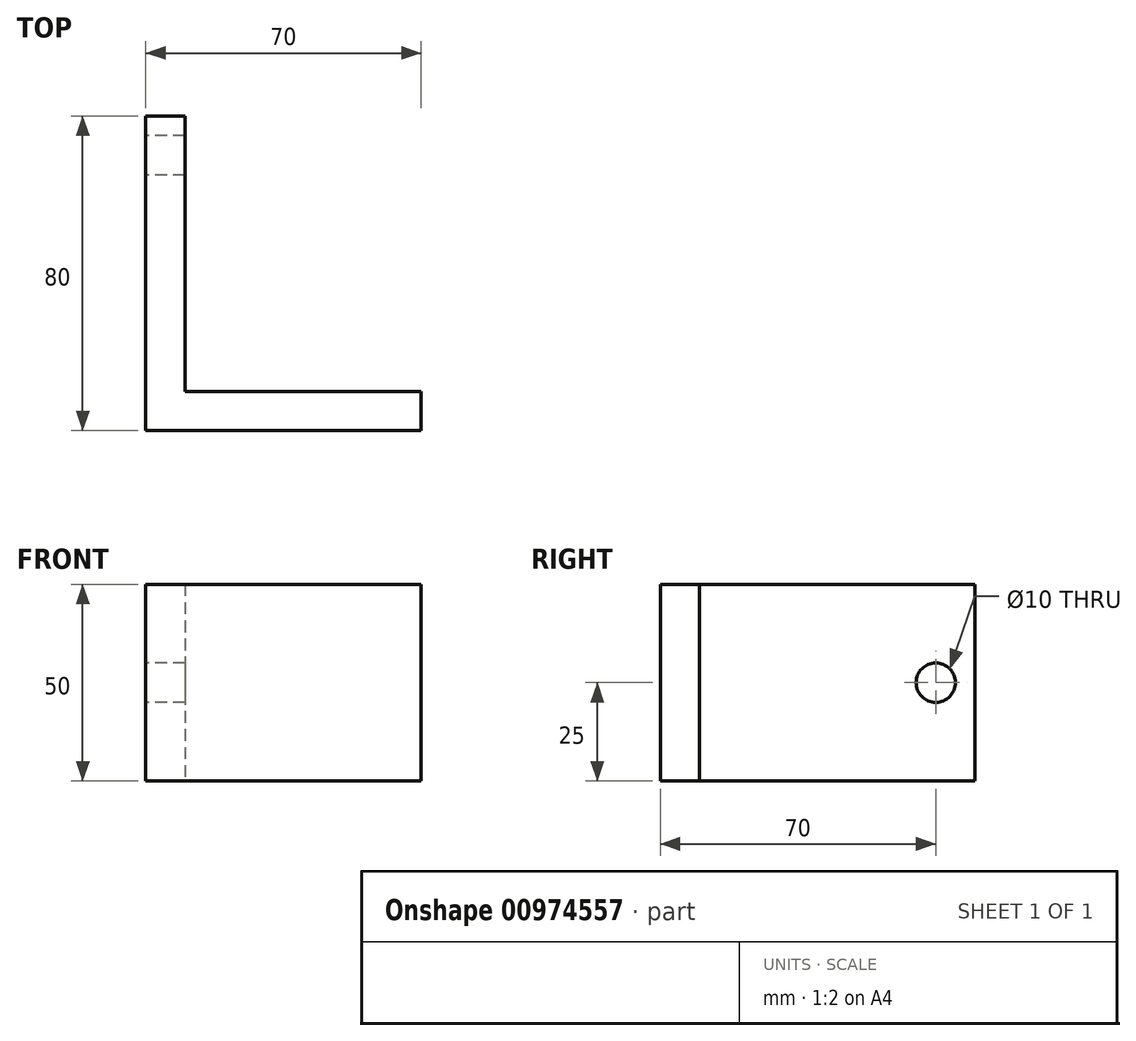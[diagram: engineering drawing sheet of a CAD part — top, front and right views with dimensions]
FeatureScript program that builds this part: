
annotation { "Feature Type Name" : "Feature", "Feature Type Description" : "" }
export const myFeature = defineFeature(function(context is Context, id is Id, definition is map)
    precondition{}
    {
        {
            var Q0;
            Q0=qCreatedBy(makeId("Front.planeOp"),FACE);
            var sketch = newSketch(context, id + "F0", { "sketchPlane" : qUnion([Q0])});
            skLineSegment(sketch, "E0.bottom", {"start": v(-70, 25) * mm, "end": v(70, 25) * mm});
            skLineSegment(sketch, "E0.top", {"start": v(-70, -25) * mm, "end": v(70, -25) * mm});
            skLineSegment(sketch, "E0.left", {"start": v(-70, 25) * mm, "end": v(-70, -25) * mm});
            skLineSegment(sketch, "E0.right", {"start": v(70, 25) * mm, "end": v(70, -25) * mm});
            skSolve(sketch);
        }
        {
            var Q0;
            Q0 = qSketchRegion(id + "F0", true);
            extrude(context, id + "F1", {"entities" : qUnion([Q0]), "depth" : 10 * mm, "offsetDistance" : 25 * mm});
        }
        {
            var Q0;
            Q0=makeQuery(id+"F1.opExtrude","CAP_FACE",FACE,{"disambiguationData":[OSD([sQuery(id+"F0.wireOp",EDGE,"E0.bottom"),sQuery(id+"F0.wireOp",EDGE,"E0.top"),sQuery(id+"F0.wireOp",EDGE,"E0.left"),sQuery(id+"F0.wireOp",EDGE,"E0.right")])],"isStart":true});
            var sketch = newSketch(context, id + "F2", { "sketchPlane" : qUnion([Q0])});
            skLineSegment(sketch, "E1.bottom", {"start": v(-70, 25) * mm, "end": v(-60, 25) * mm});
            skLineSegment(sketch, "E1.top", {"start": v(-70, -25) * mm, "end": v(-60, -25) * mm});
            skLineSegment(sketch, "E1.left", {"start": v(-70, 25) * mm, "end": v(-70, -25) * mm});
            skLineSegment(sketch, "E1.right", {"start": v(-60, 25) * mm, "end": v(-60, -25) * mm});
            skLineSegment(sketch, "E2.bottom", {"start": v(70, 25) * mm, "end": v(60, 25) * mm});
            skLineSegment(sketch, "E2.top", {"start": v(70, -25) * mm, "end": v(60, -25) * mm});
            skLineSegment(sketch, "E2.left", {"start": v(70, 25) * mm, "end": v(70, -25) * mm});
            skLineSegment(sketch, "E2.right", {"start": v(60, 25) * mm, "end": v(60, -25) * mm});
            skSolve(sketch);
        }
        {
            var Q0;
            Q0 = qSketchRegion(id + "F2", true);
            extrude(context, id + "F3", {"entities" : qUnion([Q0]), "operationType" : NewBodyOperationType.ADD, "depth" : 70 * mm, "offsetDistance" : 25 * mm});
        }
        {
            var Q0;
            Q0=makeQuery(id+"F3.boolean.opBoolean","MERGE",FACE,{"derivedFrom":[makeQuery(id+"F1.opExtrude","SWEPT_FACE",FACE,{"disambiguationData":[OSD([sQuery(id+"F0.wireOp",EDGE,"E0.left")])]}),makeQuery(id+"F3.opExtrude","SWEPT_FACE",FACE,{"disambiguationData":[OSD([sQuery(id+"F2.wireOp",EDGE,"E2.left")])]})]});
            var sketch = newSketch(context, id + "F4", { "sketchPlane" : qUnion([Q0])});
            skCircle(sketch, "E3", {"center": v(-60, 0) * mm, "radius": 5 * mm});
            skSolve(sketch);
        }
        {
            var Q0;
            Q0 = qSketchRegion(id + "F4", true);
            extrude(context, id + "F5", {"entities" : qUnion([Q0]), "operationType" : NewBodyOperationType.REMOVE, "endBound" : BoundingType.THROUGH_ALL, "oppositeDirection" : true, "depth" : 25 * mm, "offsetDistance" : 25 * mm});
        }
        {
            var Q0;
            Q0=makeQuery(id+"F3.boolean.opBoolean","MERGE",FACE,{"derivedFrom":[makeQuery(id+"F1.opExtrude","SWEPT_FACE",FACE,{"disambiguationData":[OSD([sQuery(id+"F0.wireOp",EDGE,"E0.top")])]}),makeQuery(id+"F3.opExtrude","SWEPT_FACE",FACE,{"disambiguationData":[OSD([sQuery(id+"F2.wireOp",EDGE,"E1.top")])]}),makeQuery(id+"F3.opExtrude","SWEPT_FACE",FACE,{"disambiguationData":[OSD([sQuery(id+"F2.wireOp",EDGE,"E2.top")])]})]});
            var sketch = newSketch(context, id + "F6", { "sketchPlane" : qUnion([Q0])});
            skLineSegment(sketch, "E4.bottom", {"start": v(0, 75.65) * mm, "end": v(140.09, 75.65) * mm});
            skLineSegment(sketch, "E4.top", {"start": v(0, -84.04) * mm, "end": v(140.09, -84.04) * mm});
            skLineSegment(sketch, "E4.left", {"start": v(0, 75.65) * mm, "end": v(0, -84.04) * mm});
            skLineSegment(sketch, "E4.right", {"start": v(140.09, 75.65) * mm, "end": v(140.09, -84.04) * mm});
            skSolve(sketch);
        }
        {
            var Q0;
            Q0 = qSketchRegion(id + "F6", true);
            extrude(context, id + "F7", {"entities" : qUnion([Q0]), "operationType" : NewBodyOperationType.REMOVE, "endBound" : BoundingType.THROUGH_ALL, "oppositeDirection" : true, "depth" : 25 * mm, "offsetDistance" : 25 * mm});
        }
    });
